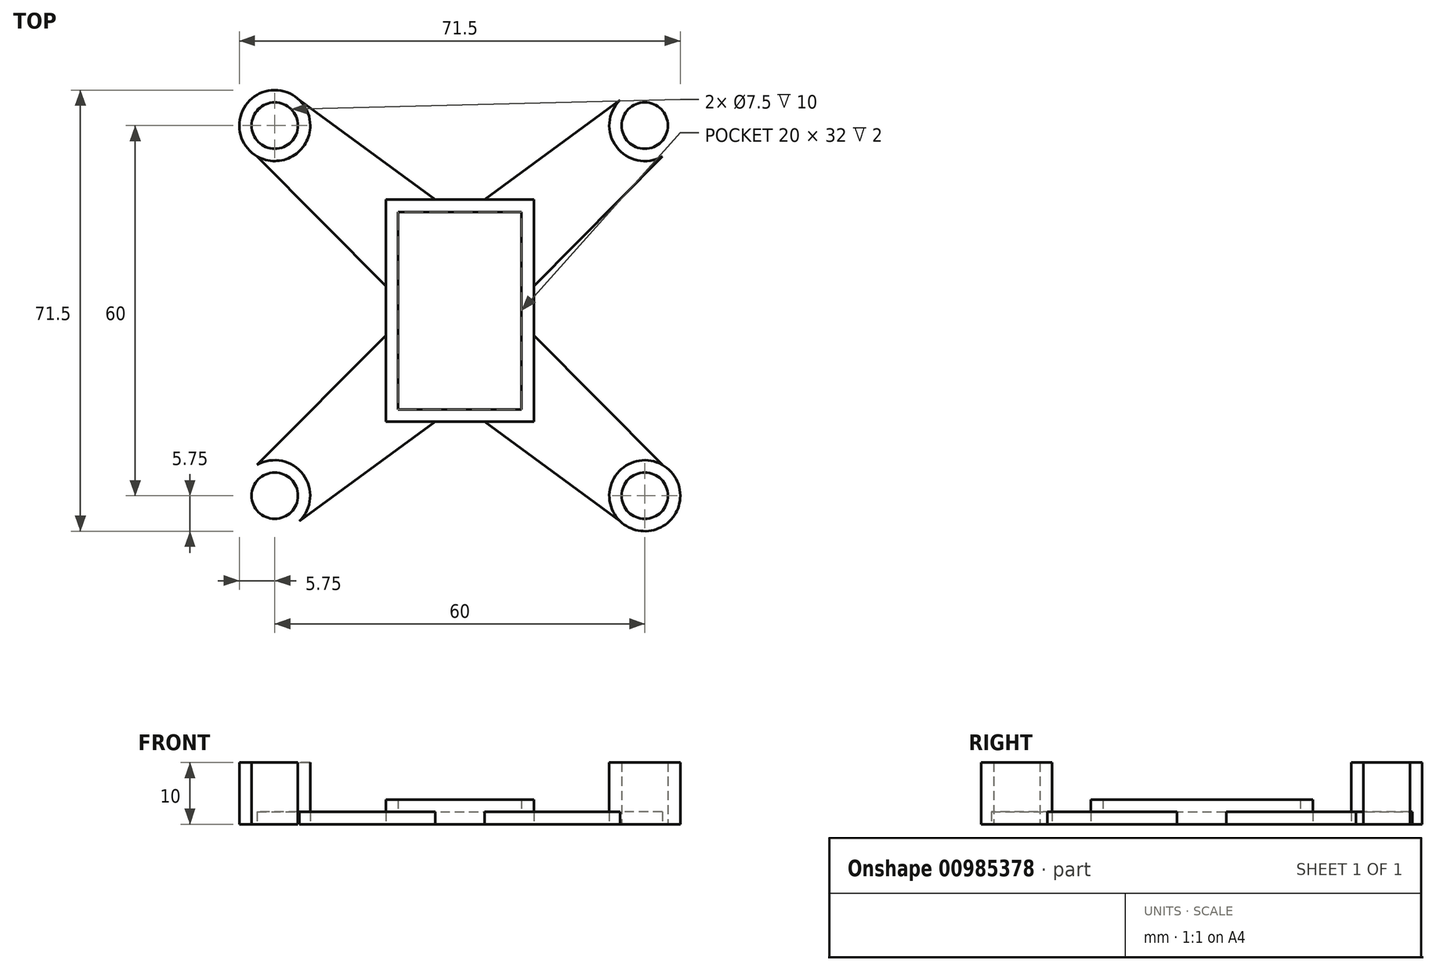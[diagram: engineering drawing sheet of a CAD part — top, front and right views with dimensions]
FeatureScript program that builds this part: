
annotation { "Feature Type Name" : "Feature", "Feature Type Description" : "" }
export const myFeature = defineFeature(function(context is Context, id is Id, definition is map)
    precondition{}
    {
        {
            var Q0;
            Q0=qCreatedBy(makeId("Top.planeOp"),FACE);
            var sketch = newSketch(context, id + "F0", { "sketchPlane" : qUnion([Q0])});
            skLineSegment(sketch, "E0.bottom", {"start": v(30, 30) * mm, "end": v(-30, 30) * mm, "construction": true});
            skLineSegment(sketch, "E0.top", {"start": v(30, -30) * mm, "end": v(-30, -30) * mm, "construction": true});
            skLineSegment(sketch, "E0.left", {"start": v(30, 30) * mm, "end": v(30, -30) * mm, "construction": true});
            skLineSegment(sketch, "E0.right", {"start": v(-30, 30) * mm, "end": v(-30, -30) * mm, "construction": true});
            skPoint(sketch, "E0.middle", {"position": v(0, 0) * mm});
            skLineSegment(sketch, "E1.bottom", {"start": v(10, 16) * mm, "end": v(-10, 16) * mm});
            skLineSegment(sketch, "E1.top", {"start": v(10, -16) * mm, "end": v(-10, -16) * mm});
            skLineSegment(sketch, "E1.left", {"start": v(10, 16) * mm, "end": v(10, -16) * mm});
            skLineSegment(sketch, "E1.right", {"start": v(-10, 16) * mm, "end": v(-10, -16) * mm});
            skLineSegment(sketch, "E2.bottom", {"start": v(12, 18) * mm, "end": v(-12, 18) * mm});
            skLineSegment(sketch, "E2.top", {"start": v(12, -18) * mm, "end": v(-12, -18) * mm});
            skLineSegment(sketch, "E2.left", {"start": v(12, 18) * mm, "end": v(12, -18) * mm});
            skLineSegment(sketch, "E2.right", {"start": v(-12, 18) * mm, "end": v(-12, -18) * mm});
            skCircle(sketch, "E3", {"center": v(-30, 30) * mm, "radius": 3.75 * mm});
            skCircle(sketch, "E4", {"center": v(-30, 30) * mm, "radius": 5.75 * mm});
            skCircle(sketch, "E5.MirrorC", {"center": v(30, 30) * mm, "radius": 3.75 * mm});
            skCircle(sketch, "E6.MirrorC", {"center": v(30, 30) * mm, "radius": 5.75 * mm});
            skCircle(sketch, "E7.MirrorC", {"center": v(30, -30) * mm, "radius": 5.75 * mm});
            skCircle(sketch, "E8.MirrorC", {"center": v(30, -30) * mm, "radius": 3.75 * mm});
            skCircle(sketch, "E9.MirrorC", {"center": v(-30, -30) * mm, "radius": 3.75 * mm});
            skCircle(sketch, "E10.MirrorC", {"center": v(-30, -30) * mm, "radius": 5.75 * mm});
            skLineSegment(sketch, "E11", {"start": v(-26, 34.13) * mm, "end": v(-4, 18) * mm});
            skLineSegment(sketch, "E12", {"start": v(-32.84, 25) * mm, "end": v(-12, 4) * mm});
            skLineSegment(sketch, "E13.MirrorCS", {"start": v(26, 34.13) * mm, "end": v(4, 18) * mm});
            skLineSegment(sketch, "E14.MirrorCS", {"start": v(32.84, 25) * mm, "end": v(12, 4) * mm});
            skLineSegment(sketch, "E15.MirrorCS", {"start": v(32.84, -25) * mm, "end": v(12, -4) * mm});
            skLineSegment(sketch, "E16.MirrorCS", {"start": v(26, -34.13) * mm, "end": v(4, -18) * mm});
            skLineSegment(sketch, "E17.MirrorCS", {"start": v(-32.84, -25) * mm, "end": v(-12, -4) * mm});
            skLineSegment(sketch, "E18.MirrorCS", {"start": v(-26, -34.13) * mm, "end": v(-4, -18) * mm});
            skSolve(sketch);
        }
        {
            var Q0;
            {var subQ0=sQuery(id+"F0.wireOp",EDGE,"E11");Q0=makeQuery(id+"F0.imprint","IMPRINT",FACE,{"disambiguationData":[TD([[makeQuery(id+"F0.imprint","IMPRINT",EDGE,{"derivedFrom":subQ0}),-1.0]])]});}
            var Q1;
            Q1=makeQuery(id+"F0.imprint","IMPRINT",FACE,{"disambiguationData":[TD([[makeQuery(id+"F0.imprint","IMPRINT",EDGE,{"derivedFrom":sQuery(id+"F0.wireOp",EDGE,"E3")}),-1.0]])]});
            var Q2;
            Q2=makeQuery(id+"F0.imprint","IMPRINT",FACE,{"disambiguationData":[TD([[makeQuery(id+"F0.imprint","IMPRINT",EDGE,{"derivedFrom":sQuery(id+"F0.wireOp",EDGE,"E5.MirrorC")}),1.0]])]});
            var Q3;
            {var subQ0=sQuery(id+"F0.wireOp",EDGE,"E13.MirrorCS");Q3=makeQuery(id+"F0.imprint","IMPRINT",FACE,{"disambiguationData":[TD([[makeQuery(id+"F0.imprint","IMPRINT",EDGE,{"derivedFrom":subQ0}),1.0]])]});}
            var Q4;
            Q4=makeQuery(id+"F0.imprint","IMPRINT",FACE,{"disambiguationData":[TD([[makeQuery(id+"F0.imprint","IMPRINT",EDGE,{"derivedFrom":sQuery(id+"F0.wireOp",EDGE,"E1.bottom")}),1.0]])]});
            var Q5;
            {var subQ0=sQuery(id+"F0.wireOp",EDGE,"E15.MirrorCS");Q5=makeQuery(id+"F0.imprint","IMPRINT",FACE,{"disambiguationData":[TD([[makeQuery(id+"F0.imprint","IMPRINT",EDGE,{"derivedFrom":subQ0}),1.0]])]});}
            var Q6;
            {var subQ0=sQuery(id+"F0.wireOp",EDGE,"E17.MirrorCS");Q6=makeQuery(id+"F0.imprint","IMPRINT",FACE,{"disambiguationData":[TD([[makeQuery(id+"F0.imprint","IMPRINT",EDGE,{"derivedFrom":subQ0}),-1.0]])]});}
            var Q7;
            Q7=makeQuery(id+"F0.imprint","IMPRINT",FACE,{"disambiguationData":[TD([[makeQuery(id+"F0.imprint","IMPRINT",EDGE,{"derivedFrom":sQuery(id+"F0.wireOp",EDGE,"E9.MirrorC")}),1.0]])]});
            var Q8;
            Q8=makeQuery(id+"F0.imprint","IMPRINT",FACE,{"disambiguationData":[TD([[makeQuery(id+"F0.imprint","IMPRINT",EDGE,{"derivedFrom":sQuery(id+"F0.wireOp",EDGE,"E1.bottom")}),-1.0]])]});
            extrude(context, id + "F1", {"entities" : qUnion([Q0, Q1, Q2, Q3, Q4, Q5, Q6, Q7, Q8]), "depth" : 2 * mm, "offsetDistance" : 25 * mm});
        }
        {
            var Q0;
            Q0=makeQuery(id+"F0.imprint","IMPRINT",FACE,{"disambiguationData":[TD([[makeQuery(id+"F0.imprint","IMPRINT",EDGE,{"derivedFrom":sQuery(id+"F0.wireOp",EDGE,"E3")}),-1.0]])]});
            var Q1;
            Q1=makeQuery(id+"F0.imprint","IMPRINT",FACE,{"disambiguationData":[TD([[makeQuery(id+"F0.imprint","IMPRINT",EDGE,{"derivedFrom":sQuery(id+"F0.wireOp",EDGE,"E5.MirrorC")}),1.0]])]});
            var Q2;
            Q2=makeQuery(id+"F0.imprint","IMPRINT",FACE,{"disambiguationData":[TD([[makeQuery(id+"F0.imprint","IMPRINT",EDGE,{"derivedFrom":sQuery(id+"F0.wireOp",EDGE,"E8.MirrorC")}),-1.0]])]});
            var Q3;
            Q3=makeQuery(id+"F0.imprint","IMPRINT",FACE,{"disambiguationData":[TD([[makeQuery(id+"F0.imprint","IMPRINT",EDGE,{"derivedFrom":sQuery(id+"F0.wireOp",EDGE,"E9.MirrorC")}),1.0]])]});
            extrude(context, id + "F2", {"entities" : qUnion([Q0, Q1, Q2, Q3]), "operationType" : NewBodyOperationType.ADD, "depth" : 10 * mm, "offsetDistance" : 25 * mm});
        }
        {
            var Q0;
            Q0=makeQuery(id+"F0.imprint","IMPRINT",FACE,{"disambiguationData":[TD([[makeQuery(id+"F0.imprint","IMPRINT",EDGE,{"derivedFrom":sQuery(id+"F0.wireOp",EDGE,"E1.bottom")}),-1.0]])]});
            extrude(context, id + "F3", {"entities" : qUnion([Q0]), "operationType" : NewBodyOperationType.ADD, "depth" : 4 * mm, "offsetDistance" : 25 * mm});
        }
    });
